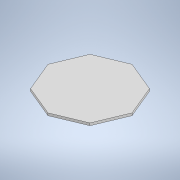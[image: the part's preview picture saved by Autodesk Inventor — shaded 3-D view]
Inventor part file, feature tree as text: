
AUTODESK INVENTOR PART (.ipt)
format: ipt  version: 2020 (Build 240168000, 168)  size: 94,208 bytes
history: native  units: mm
features: extrude x1, sketch x1
ambient origin geometry x8: Origin, YZ Plane, XZ Plane, XY Plane, X Axis, Y Axis, Z Axis, Center Point
bodies: Solide1 (feature_tree)
feature tree (2):
  extrude  "Extrusion1"  Depth=10.0mm TaperAngle=0.0deg
  sketch  "Esquisse1"
